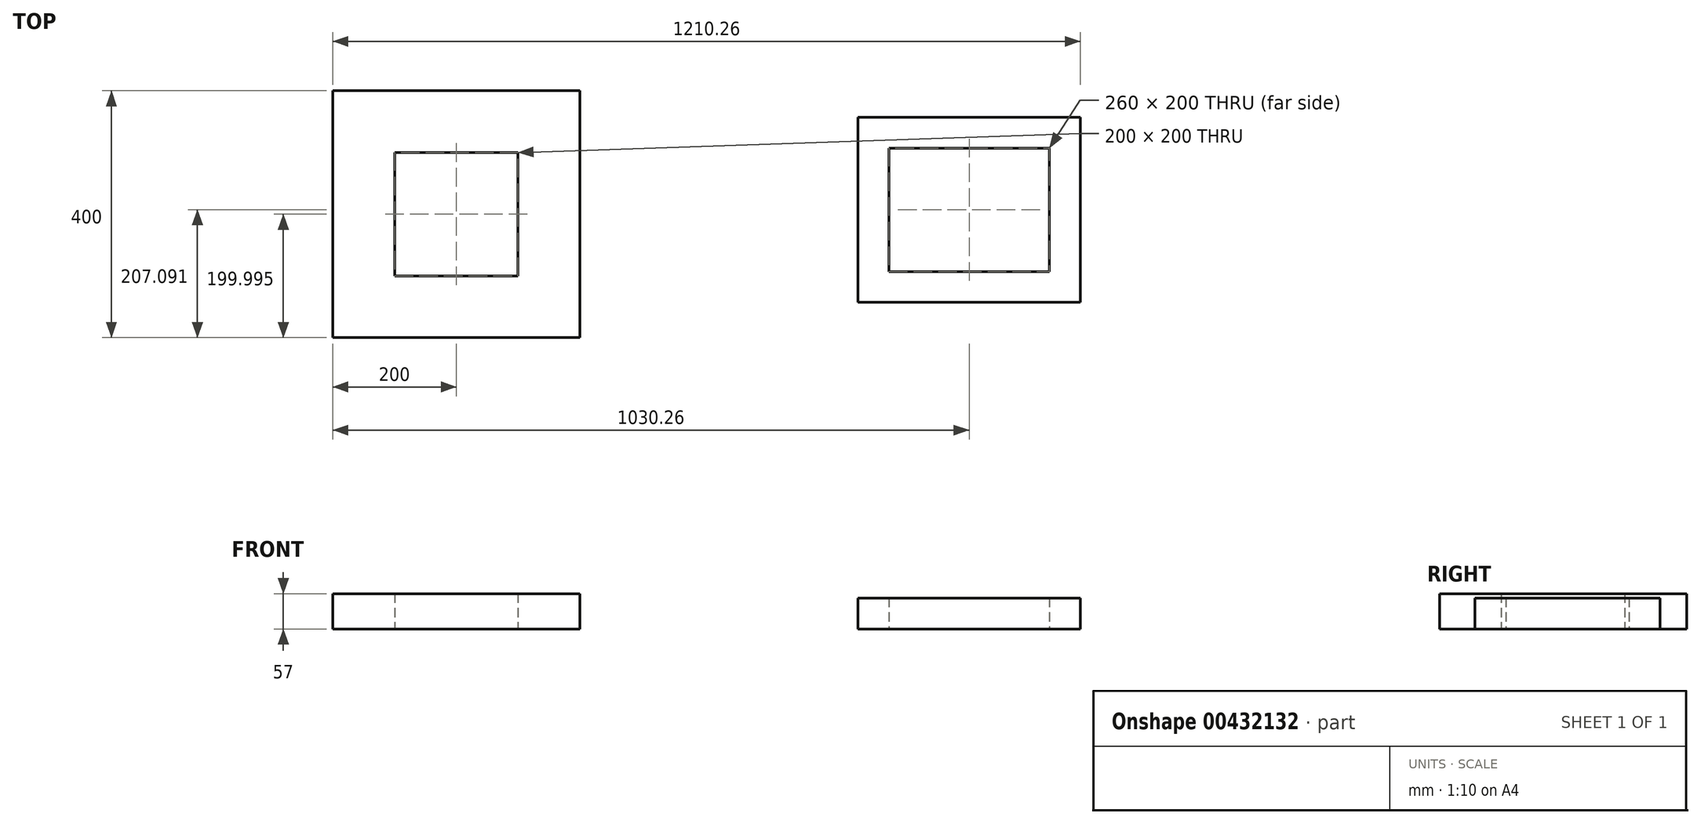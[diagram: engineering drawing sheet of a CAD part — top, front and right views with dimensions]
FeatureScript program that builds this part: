
annotation { "Feature Type Name" : "Feature", "Feature Type Description" : "" }
export const myFeature = defineFeature(function(context is Context, id is Id, definition is map)
    precondition{}
    {
        {
            var Q0;
            Q0=qCreatedBy(makeId("Top.planeOp"),FACE);
            var sketch = newSketch(context, id + "F0", { "sketchPlane" : qUnion([Q0])});
            skLineSegment(sketch, "E0.bottom", {"start": v(400, 191.09) * mm, "end": v(300, 191.09) * mm});
            skLineSegment(sketch, "E0.top", {"start": v(400, -208.91) * mm, "end": v(300, -208.91) * mm});
            skLineSegment(sketch, "E0.left", {"start": v(400, 191.09) * mm, "end": v(400, -208.91) * mm});
            skLineSegment(sketch, "E0.right", {"start": v(300, 191.09) * mm, "end": v(300, -208.91) * mm});
            skLineSegment(sketch, "E1.bottom", {"start": v(300, -208.91) * mm, "end": v(100, -208.91) * mm});
            skLineSegment(sketch, "E1.top", {"start": v(300, -108.91) * mm, "end": v(100, -108.91) * mm});
            skLineSegment(sketch, "E1.left", {"start": v(300, -208.91) * mm, "end": v(300, -108.91) * mm});
            skLineSegment(sketch, "E1.right", {"start": v(100, -208.91) * mm, "end": v(100, -108.91) * mm});
            skLineSegment(sketch, "E2.bottom", {"start": v(100, -208.91) * mm, "end": v(0, -208.91) * mm});
            skLineSegment(sketch, "E2.top", {"start": v(100, 191.09) * mm, "end": v(0, 191.09) * mm});
            skLineSegment(sketch, "E2.left", {"start": v(100, -208.91) * mm, "end": v(100, 191.09) * mm});
            skLineSegment(sketch, "E2.right", {"start": v(0, -208.91) * mm, "end": v(0, 191.09) * mm});
            skLineSegment(sketch, "E3.bottom", {"start": v(100, 191.09) * mm, "end": v(300, 191.09) * mm});
            skLineSegment(sketch, "E3.top", {"start": v(100, 91.09) * mm, "end": v(300, 91.09) * mm});
            skLineSegment(sketch, "E3.left", {"start": v(100, 191.09) * mm, "end": v(100, 91.09) * mm});
            skLineSegment(sketch, "E3.right", {"start": v(300, 191.09) * mm, "end": v(300, 91.09) * mm});
            skSolve(sketch);
        }
        {
            var Q0;
            {var subQ0=sQuery(id+"F0.wireOp",EDGE,"E3.bottom");var subQ2=sQuery(id+"F0.wireOp",EDGE,"E0.bottom");var subQ10=sQuery(id+"F0.wireOp",EDGE,"E1.bottom");var subQ15=sQuery(id+"F0.wireOp",EDGE,"E1.right");var subQ16=makeQuery(id+"F0.imprint","IMPRINT",EDGE,{"derivedFrom":subQ15});Q0=qUnion([makeQuery(id+"F0.imprint","IMPRINT",FACE,{"disambiguationData":[TD([[subQ16,1.0]])]}),makeQuery(id+"F0.imprint","IMPRINT",FACE,{"disambiguationData":[TD([[makeQuery(id+"F0.imprint","IMPRINT",EDGE,{"derivedFrom":subQ2}),1.0]])]}),makeQuery(id+"F0.imprint","IMPRINT",FACE,{"disambiguationData":[TD([[makeQuery(id+"F0.imprint","IMPRINT",EDGE,{"derivedFrom":subQ10}),-1.0]])]}),makeQuery(id+"F0.imprint","IMPRINT",FACE,{"disambiguationData":[TD([[makeQuery(id+"F0.imprint","IMPRINT",EDGE,{"derivedFrom":subQ0}),-1.0]])]})]);}
            extrude(context, id + "F1", {"entities" : qUnion([Q0]), "depth" : 57 * mm});
        }
        {
            var Q0;
            Q0=qCreatedBy(makeId("Top.planeOp"),FACE);
            var sketch = newSketch(context, id + "F2", { "sketchPlane" : qUnion([Q0])});
            skLineSegment(sketch, "E4.bottom", {"start": v(850.26, 148.18) * mm, "end": v(900.26, 148.18) * mm});
            skLineSegment(sketch, "E4.top", {"start": v(850.26, -151.82) * mm, "end": v(900.26, -151.82) * mm});
            skLineSegment(sketch, "E4.left", {"start": v(850.26, 148.18) * mm, "end": v(850.26, -151.82) * mm});
            skLineSegment(sketch, "E4.right", {"start": v(900.26, 148.18) * mm, "end": v(900.26, -151.82) * mm});
            skLineSegment(sketch, "E5.bottom", {"start": v(850.26, 148.18) * mm, "end": v(1210.26, 148.18) * mm});
            skLineSegment(sketch, "E5.top", {"start": v(850.26, 98.18) * mm, "end": v(1210.26, 98.18) * mm});
            skLineSegment(sketch, "E5.left", {"start": v(850.26, 148.18) * mm, "end": v(850.26, 98.18) * mm});
            skLineSegment(sketch, "E5.right", {"start": v(1210.26, 148.18) * mm, "end": v(1210.26, 98.18) * mm});
            skLineSegment(sketch, "E6.bottom", {"start": v(850.26, -151.82) * mm, "end": v(1210.26, -151.82) * mm});
            skLineSegment(sketch, "E6.top", {"start": v(850.26, -101.82) * mm, "end": v(1210.26, -101.82) * mm});
            skLineSegment(sketch, "E6.left", {"start": v(850.26, -151.82) * mm, "end": v(850.26, -101.82) * mm});
            skLineSegment(sketch, "E6.right", {"start": v(1210.26, -151.82) * mm, "end": v(1210.26, -101.82) * mm});
            skLineSegment(sketch, "E7.bottom", {"start": v(1210.26, 148.18) * mm, "end": v(1160.26, 148.18) * mm});
            skLineSegment(sketch, "E7.top", {"start": v(1210.26, -151.82) * mm, "end": v(1160.26, -151.82) * mm});
            skLineSegment(sketch, "E7.left", {"start": v(1210.26, 148.18) * mm, "end": v(1210.26, -151.82) * mm});
            skLineSegment(sketch, "E7.right", {"start": v(1160.26, 148.18) * mm, "end": v(1160.26, -151.82) * mm});
            skSolve(sketch);
        }
        {
            var Q0;
            Q0 = qSketchRegion(id + "F2", true);
            extrude(context, id + "F3", {"entities" : qUnion([Q0]), "depth" : 50 * mm});
        }
    });
